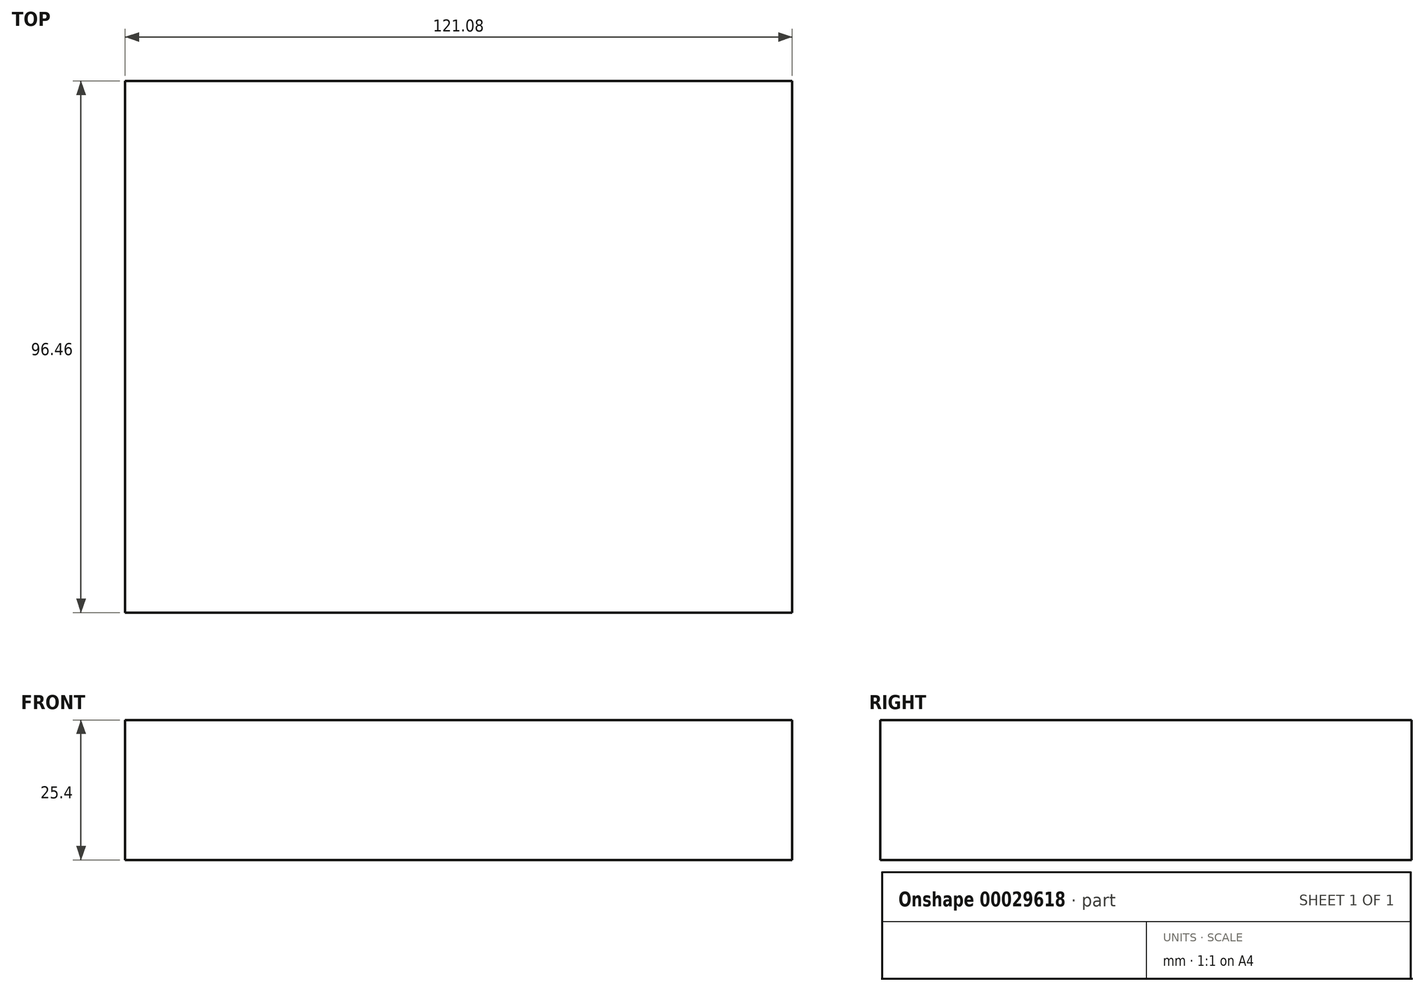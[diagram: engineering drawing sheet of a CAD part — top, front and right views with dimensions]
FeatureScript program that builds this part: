
annotation { "Feature Type Name" : "Feature", "Feature Type Description" : "" }
export const myFeature = defineFeature(function(context is Context, id is Id, definition is map)
    precondition{}
    {
        {
            var Q0;
            Q0=qCreatedBy(makeId("Top.planeOp"),FACE);
            var sketch = newSketch(context, id + "F0", { "sketchPlane" : qUnion([Q0])});
            skLineSegment(sketch, "E0.bottom", {"start": v(-68.16, -27.9) * mm, "end": v(52.92, -27.9) * mm});
            skLineSegment(sketch, "E0.top", {"start": v(-68.16, 68.56) * mm, "end": v(52.92, 68.56) * mm});
            skLineSegment(sketch, "E0.left", {"start": v(-68.16, -27.9) * mm, "end": v(-68.16, 68.56) * mm});
            skLineSegment(sketch, "E0.right", {"start": v(52.92, -27.9) * mm, "end": v(52.92, 68.56) * mm});
            skSolve(sketch);
        }
        {
            var Q0;
            Q0=makeQuery(id+"F0.imprint","IMPRINT",FACE,{"disambiguationData":[TD([[makeQuery(id+"F0.imprint","IMPRINT",EDGE,{"derivedFrom":sQuery(id+"F0.wireOp",EDGE,"E0.bottom")}),1.0]])]});
            extrude(context, id + "F1", {"entities" : qUnion([Q0]), "depth" : 25.4 * mm});
        }
    });
